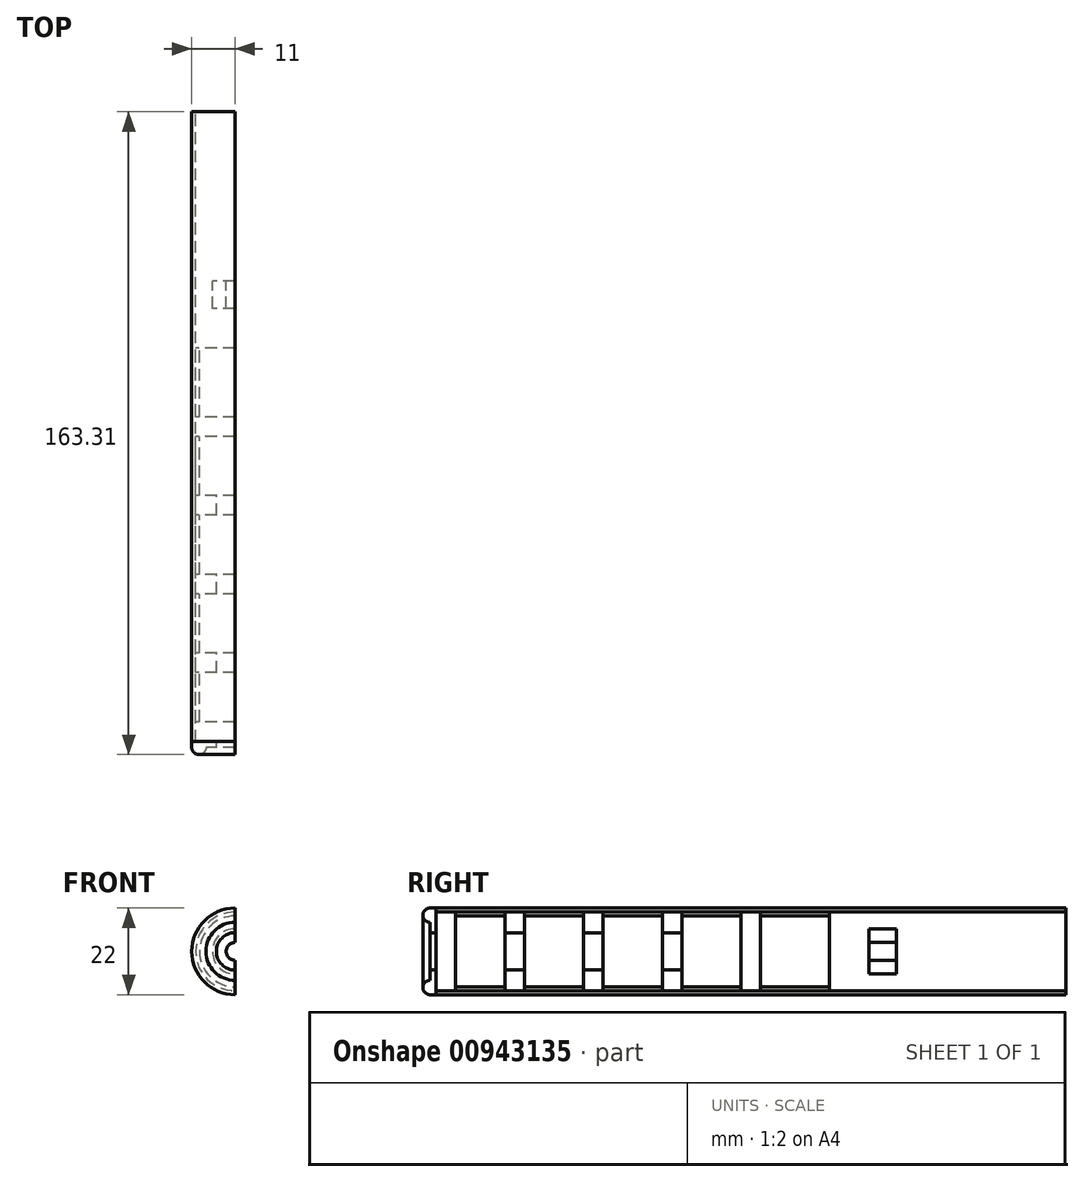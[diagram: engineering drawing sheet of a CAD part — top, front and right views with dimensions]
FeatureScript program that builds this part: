
annotation { "Feature Type Name" : "Feature", "Feature Type Description" : "" }
export const myFeature = defineFeature(function(context is Context, id is Id, definition is map)
    precondition{}
    {
        {
            var Q0;
            Q0=qCreatedBy(makeId("Right.planeOp"),FACE);
            var sketch = newSketch(context, id + "F0", { "sketchPlane" : qUnion([Q0])});
            skLineSegment(sketch, "E0", {"start": v(0, 0) * mm, "end": v(-160, 0) * mm, "construction": true});
            skLineSegment(sketch, "E1", {"start": v(0, 0) * mm, "end": v(0, 11) * mm, "construction": true});
            skLineSegment(sketch, "E2", {"start": v(0, 11) * mm, "end": v(-160, 11) * mm});
            skLineSegment(sketch, "E3", {"start": v(-160, 11) * mm, "end": v(-160, 0) * mm, "construction": true});
            skLineSegment(sketch, "E4.0", {"start": v(0, 10) * mm, "end": v(-160, 10) * mm});
            skLineSegment(sketch, "E5", {"start": v(-160, 11) * mm, "end": v(-160, 10) * mm});
            skLineSegment(sketch, "E6", {"start": v(0, 11) * mm, "end": v(0, 10) * mm});
            skLineSegment(sketch, "E7", {"start": v(-50, 11) * mm, "end": v(-50, 0) * mm, "construction": true});
            skLineSegment(sketch, "E8", {"start": v(-60, 11) * mm, "end": v(-60, 0) * mm, "construction": true});
            skLineSegment(sketch, "E9.0", {"start": v(0, 2.25) * mm, "end": v(-160, 2.25) * mm, "construction": true});
            skPoint(sketch, "E10", {"position": v(-80, 10) * mm});
            skPoint(sketch, "E11", {"position": v(-100, 10) * mm});
            skPoint(sketch, "E12", {"position": v(-120, 10) * mm});
            skPoint(sketch, "E13", {"position": v(-140, 10) * mm});
            skLineSegment(sketch, "E14.bottom", {"start": v(-82.5, 10) * mm, "end": v(-77.5, 10) * mm});
            skLineSegment(sketch, "E14.top", {"start": v(-82.5, 4.75) * mm, "end": v(-77.5, 4.75) * mm});
            skLineSegment(sketch, "E14.left", {"start": v(-82.5, 10) * mm, "end": v(-82.5, 4.75) * mm});
            skLineSegment(sketch, "E14.right", {"start": v(-77.5, 10) * mm, "end": v(-77.5, 4.75) * mm});
            skLineSegment(sketch, "E15", {"start": v(-80, 2.25) * mm, "end": v(-80, 4.75) * mm, "construction": true});
            skLineSegment(sketch, "E16.1.0.0", {"start": v(-102.5, 10) * mm, "end": v(-102.5, 4.75) * mm});
            skLineSegment(sketch, "E16.1.0.1", {"start": v(-102.5, 4.75) * mm, "end": v(-97.5, 4.75) * mm});
            skLineSegment(sketch, "E16.1.0.2", {"start": v(-97.5, 10) * mm, "end": v(-97.5, 4.75) * mm});
            skLineSegment(sketch, "E16.2.0.0", {"start": v(-122.5, 10) * mm, "end": v(-122.5, 4.75) * mm});
            skLineSegment(sketch, "E16.2.0.1", {"start": v(-122.5, 4.75) * mm, "end": v(-117.5, 4.75) * mm});
            skLineSegment(sketch, "E16.2.0.2", {"start": v(-117.5, 10) * mm, "end": v(-117.5, 4.75) * mm});
            skLineSegment(sketch, "E16.3.0.0", {"start": v(-142.5, 10) * mm, "end": v(-142.5, 4.75) * mm});
            skLineSegment(sketch, "E16.3.0.1", {"start": v(-142.5, 4.75) * mm, "end": v(-137.5, 4.75) * mm});
            skLineSegment(sketch, "E16.3.0.2", {"start": v(-137.5, 10) * mm, "end": v(-137.5, 4.75) * mm});
            skLineSegment(sketch, "E16.direction1", {"start": v(-82.5, 4.75) * mm, "end": v(-102.5, 4.75) * mm, "construction": true});
            skLineSegment(sketch, "E17.bottom", {"start": v(-160, 10) * mm, "end": v(-155, 10) * mm});
            skLineSegment(sketch, "E17.top", {"start": v(-160, 4.75) * mm, "end": v(-155, 4.75) * mm});
            skLineSegment(sketch, "E17.left", {"start": v(-160, 10) * mm, "end": v(-160, 4.75) * mm});
            skLineSegment(sketch, "E17.right", {"start": v(-155, 10) * mm, "end": v(-155, 4.75) * mm});
            skLineSegment(sketch, "E18", {"start": v(-160, 7.37) * mm, "end": v(-160, 11) * mm});
            skLineSegment(sketch, "E19.bottom", {"start": v(-160, 11) * mm, "end": v(-161.5, 11) * mm});
            skLineSegment(sketch, "E19.top", {"start": v(-160, 4.75) * mm, "end": v(-161.5, 4.75) * mm});
            skLineSegment(sketch, "E19.left", {"start": v(-160, 11) * mm, "end": v(-160, 4.75) * mm});
            skLineSegment(sketch, "E19.right", {"start": v(-161.5, 11) * mm, "end": v(-161.5, 4.75) * mm});
            skPoint(sketch, "E20.centerSnap0", {"position": v(-160, 9.19) * mm});
            skArc(sketch, "E21.trimOffspring", {"start": v(-161.5, 11) * mm, "mid": v(-163.31, 9.19) * mm, "end": v(-161.5, 7.37) * mm});
            skLineSegment(sketch, "E22.trimOffspring", {"start": v(-82.5, 9) * mm, "end": v(-97.5, 9) * mm});
            skLineSegment(sketch, "E23.trimOffspring", {"start": v(-102.5, 9) * mm, "end": v(-117.5, 9) * mm});
            skLineSegment(sketch, "E24.trimOffspring", {"start": v(-122.5, 9) * mm, "end": v(-137.5, 9) * mm});
            skLineSegment(sketch, "E25.trimOffspring", {"start": v(-142.5, 9) * mm, "end": v(-155, 9) * mm});
            skLineSegment(sketch, "E26.trimOffspring", {"start": v(-60, 9) * mm, "end": v(-77.5, 9) * mm});
            skLineSegment(sketch, "E27.bottom", {"start": v(-60, 10) * mm, "end": v(-50, 10) * mm});
            skLineSegment(sketch, "E27.top", {"start": v(-60, 2.25) * mm, "end": v(-50, 2.25) * mm});
            skLineSegment(sketch, "E27.left", {"start": v(-60, 10) * mm, "end": v(-60, 2.25) * mm});
            skLineSegment(sketch, "E27.right", {"start": v(-50, 10) * mm, "end": v(-50, 2.25) * mm});
            skLineSegment(sketch, "E28.bottom", {"start": v(-50, 2.25) * mm, "end": v(-43, 2.25) * mm});
            skLineSegment(sketch, "E28.top", {"start": v(-50, 5.75) * mm, "end": v(-43, 5.75) * mm});
            skLineSegment(sketch, "E28.left", {"start": v(-50, 2.25) * mm, "end": v(-50, 5.75) * mm});
            skLineSegment(sketch, "E28.right", {"start": v(-43, 2.25) * mm, "end": v(-43, 5.75) * mm});
            skSolve(sketch);
        }
        {
            var Q0;
            {var subQ8=sQuery(id+"F0.wireOp",EDGE,"E2");Q0=makeQuery(id+"F0.imprint","IMPRINT",FACE,{"disambiguationData":[TD([[makeQuery(id+"F0.imprint","IMPRINT",EDGE,{"derivedFrom":subQ8}),1.0]])]});}
            var Q1;
            Q1=sQuery(id+"F0.wireOp",EDGE,"E0");
            revolve(context, id + "F1", {"surfaceOperationType" : NewSurfaceOperationType.NEW, "entities" : qUnion([Q0]), "axis" : qUnion([Q1]), "revolveType" : RevolveType.FULL});
        }
        {
            var Q0;
            {var subQ5=sQuery(id+"F0.wireOp",EDGE,"E26.trimOffspring");Q0=makeQuery(id+"F0.imprint","IMPRINT",FACE,{"disambiguationData":[TD([[makeQuery(id+"F0.imprint","IMPRINT",EDGE,{"derivedFrom":subQ5}),-1.0]])]});}
            var Q1;
            {var subQ5=sQuery(id+"F0.wireOp",EDGE,"E22.trimOffspring");Q1=makeQuery(id+"F0.imprint","IMPRINT",FACE,{"disambiguationData":[TD([[makeQuery(id+"F0.imprint","IMPRINT",EDGE,{"derivedFrom":subQ5}),-1.0]])]});}
            var Q2;
            {var subQ5=sQuery(id+"F0.wireOp",EDGE,"E23.trimOffspring");Q2=makeQuery(id+"F0.imprint","IMPRINT",FACE,{"disambiguationData":[TD([[makeQuery(id+"F0.imprint","IMPRINT",EDGE,{"derivedFrom":subQ5}),-1.0]])]});}
            var Q3;
            {var subQ5=sQuery(id+"F0.wireOp",EDGE,"E25.trimOffspring");Q3=makeQuery(id+"F0.imprint","IMPRINT",FACE,{"disambiguationData":[TD([[makeQuery(id+"F0.imprint","IMPRINT",EDGE,{"derivedFrom":subQ5}),-1.0]])]});}
            var Q4;
            {var subQ5=sQuery(id+"F0.wireOp",EDGE,"E24.trimOffspring");Q4=makeQuery(id+"F0.imprint","IMPRINT",FACE,{"disambiguationData":[TD([[makeQuery(id+"F0.imprint","IMPRINT",EDGE,{"derivedFrom":subQ5}),-1.0]])]});}
            var Q5;
            Q5=sQuery(id+"F0.wireOp",EDGE,"E0");
            revolve(context, id + "F2", {"surfaceOperationType" : NewSurfaceOperationType.NEW, "entities" : qUnion([Q0, Q1, Q2, Q3, Q4]), "axis" : qUnion([Q5]), "revolveType" : RevolveType.FULL});
        }
        {
            var Q0;
            {var subQ3=sQuery(id+"F0.wireOp",EDGE,"E27.bottom");Q0=makeQuery(id+"F0.imprint","IMPRINT",FACE,{"disambiguationData":[TD([[makeQuery(id+"F0.imprint","IMPRINT",EDGE,{"derivedFrom":subQ3}),-1.0]])]});}
            var Q1;
            {var subQ3=sQuery(id+"F0.wireOp",EDGE,"E14.bottom");Q1=makeQuery(id+"F0.imprint","IMPRINT",FACE,{"disambiguationData":[TD([[makeQuery(id+"F0.imprint","IMPRINT",EDGE,{"derivedFrom":subQ3}),-1.0]])]});}
            var Q2;
            {var subQ0=sQuery(id+"F0.wireOp",EDGE,"E16.1.0.1");Q2=makeQuery(id+"F0.imprint","IMPRINT",FACE,{"disambiguationData":[TD([[makeQuery(id+"F0.imprint","IMPRINT",EDGE,{"derivedFrom":subQ0}),1.0]])]});}
            var Q3;
            {var subQ0=sQuery(id+"F0.wireOp",EDGE,"E16.2.0.1");Q3=makeQuery(id+"F0.imprint","IMPRINT",FACE,{"disambiguationData":[TD([[makeQuery(id+"F0.imprint","IMPRINT",EDGE,{"derivedFrom":subQ0}),1.0]])]});}
            var Q4;
            {var subQ0=sQuery(id+"F0.wireOp",EDGE,"E16.3.0.1");Q4=makeQuery(id+"F0.imprint","IMPRINT",FACE,{"disambiguationData":[TD([[makeQuery(id+"F0.imprint","IMPRINT",EDGE,{"derivedFrom":subQ0}),1.0]])]});}
            var Q5;
            {var subQ3=sQuery(id+"F0.wireOp",EDGE,"E17.bottom");Q5=makeQuery(id+"F0.imprint","IMPRINT",FACE,{"disambiguationData":[TD([[makeQuery(id+"F0.imprint","IMPRINT",EDGE,{"derivedFrom":subQ3}),-1.0]])]});}
            var Q6;
            Q6=makeQuery(id+"F0.imprint","IMPRINT",FACE,{"disambiguationData":[TD([[makeQuery(id+"F0.imprint","IMPRINT",EDGE,{"derivedFrom":sQuery(id+"F0.wireOp",EDGE,"E28.bottom")}),1.0]])]});
            var Q7;
            {var subQ3=sQuery(id+"F0.wireOp",EDGE,"E19.bottom");Q7=makeQuery(id+"F0.imprint","IMPRINT",FACE,{"disambiguationData":[TD([[makeQuery(id+"F0.imprint","IMPRINT",EDGE,{"derivedFrom":subQ3}),1.0]])]});}
            var Q8;
            {var subQ0=sQuery(id+"F0.wireOp",EDGE,"E21.trimOffspring");Q8=makeQuery(id+"F0.imprint","IMPRINT",FACE,{"disambiguationData":[TD([[makeQuery(id+"F0.imprint","IMPRINT",EDGE,{"derivedFrom":subQ0}),1.0]])]});}
            var Q9;
            Q9=sQuery(id+"F0.wireOp",EDGE,"E0");
            revolve(context, id + "F3", {"surfaceOperationType" : NewSurfaceOperationType.NEW, "entities" : qUnion([Q0, Q1, Q2, Q3, Q4, Q5, Q6, Q7, Q8]), "axis" : qUnion([Q9]), "revolveType" : RevolveType.FULL});
        }
        {
            var Q0;
            Q0=qCreatedBy(makeId("Right.planeOp"),FACE);
            var sketch = newSketch(context, id + "F4", { "sketchPlane" : qUnion([Q0])});
            skLineSegment(sketch, "E29.bottom", {"start": v(-174.36, 19.78) * mm, "end": v(15.96, 19.78) * mm});
            skLineSegment(sketch, "E29.top", {"start": v(-174.36, -18.98) * mm, "end": v(15.96, -18.98) * mm});
            skLineSegment(sketch, "E29.left", {"start": v(-174.36, 19.78) * mm, "end": v(-174.36, -18.98) * mm});
            skLineSegment(sketch, "E29.right", {"start": v(15.96, 19.78) * mm, "end": v(15.96, -18.98) * mm});
            skSolve(sketch);
        }
        {
            var Q0;
            Q0=makeQuery(id+"F4.imprint","IMPRINT",FACE,{"disambiguationData":[TD([[makeQuery(id+"F4.imprint","IMPRINT",EDGE,{"derivedFrom":sQuery(id+"F4.wireOp",EDGE,"E29.bottom")}),-1.0]])]});
            extrude(context, id + "F5", {"entities" : qUnion([Q0]), "operationType" : NewBodyOperationType.REMOVE, "depth" : 25 * mm, "offsetDistance" : 25 * mm});
        }
    });
